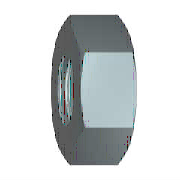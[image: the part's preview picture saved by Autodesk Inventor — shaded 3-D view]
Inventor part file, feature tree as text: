
AUTODESK INVENTOR PART (.ipt)
format: ipt  version: 2015 (Build 190159000, 159)  size: 164,352 bytes
history: native  units: mm (DEFAULTED — no unit token found)
features: sketch x3, other x2, extrude x1, hole x1, plane x1
ambient origin geometry x7: Origin, YZ Plane, XZ Plane, X Axis, Y Axis, Z Axis, Center Point
bodies: Body1 (feature_tree)
feature tree (8):
  extrude  "Bryła"  Depth=20.78461mm
  other  "Faza1"
  hole  "Gwint"  [1 undecoded]
  other  "Work Axis1"
  plane  "Work Plane1"
  sketch  "Szkic1"
  sketch  "Szkic2"
  sketch  "Szkic3"
note: 1 required parameter value undecoded (feature->parameter linkage not recoverable at this tier; creation-order binding heuristic only, values carry confidence <= 0.55)
